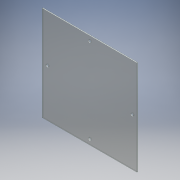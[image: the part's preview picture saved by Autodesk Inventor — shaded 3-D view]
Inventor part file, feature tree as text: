
AUTODESK INVENTOR PART (.ipt)
format: ipt  version: 2016 (Build 200138000, 138)  size: 104,960 bytes
history: native  units: mm
features: sketch x2, extrude x1, hole x1, projected_geometry x1
ambient origin geometry x8: Origin, YZ Plane, XZ Plane, XY Plane, X Axis, Y Axis, Z Axis, Center Point
bodies: Solid1 (feature_tree)
feature tree (5):
  extrude  "Extrusion1"  Depth=1.5875mm TaperAngle=0.0deg
  hole  "Hole1"  [1 undecoded]
  sketch  "Sketch1"  dims[d0=190.0mm d1=1.5875mm d2=0.0mm]
  sketch  "Sketch2"  dims[d7=5.5mm d8=6.0mm d9=10.4mm d10=2.0mm d11=90.0deg d12=8.0mm d13=20.594885mm d17=10.0mm d18=10.0mm d19=10.0mm d20=10.0mm]
  projected_geometry  "Projected Loop1"
note: 1 required parameter value undecoded (feature->parameter linkage not recoverable at this tier; creation-order binding heuristic only, values carry confidence <= 0.55)
